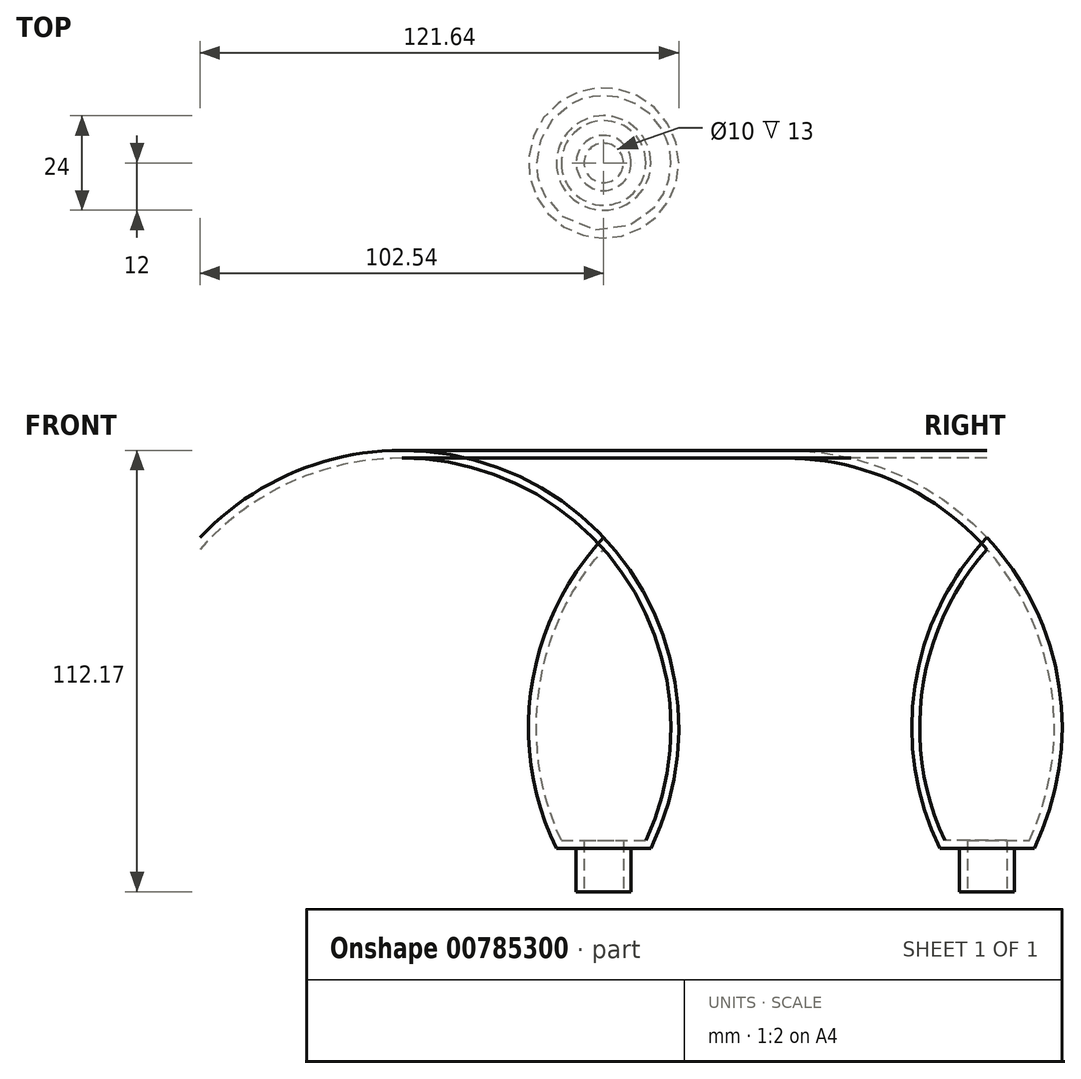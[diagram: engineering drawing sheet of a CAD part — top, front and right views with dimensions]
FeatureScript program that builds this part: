
annotation { "Feature Type Name" : "Feature", "Feature Type Description" : "" }
export const myFeature = defineFeature(function(context is Context, id is Id, definition is map)
    precondition{}
    {
        {
            var Q0;
            Q0=qCreatedBy(makeId("Front.planeOp"),FACE);
            var sketch = newSketch(context, id + "F0", { "sketchPlane" : qUnion([Q0])});
            skLineSegment(sketch, "E0", {"start": v(0, 0) * mm, "end": v(0, 90) * mm});
            skLineSegment(sketch, "E1", {"start": v(5, 0) * mm, "end": v(22.78, 0) * mm});
            skLineSegment(sketch, "E2", {"start": v(5, 0) * mm, "end": v(5, 13) * mm});
            skLineSegment(sketch, "E3", {"start": v(5, 13) * mm, "end": v(10.74, 13) * mm});
            skArc(sketch, "E4", {"start": v(10.74, 13) * mm, "mid": v(16.4, 51.61) * mm, "end": v(0, 87.03) * mm});
            skArc(sketch, "E5.0", {"start": v(12, 11) * mm, "mid": v(18.3, 52.37) * mm, "end": v(0, 90) * mm});
            skLineSegment(sketch, "E5.1", {"start": v(7, 11) * mm, "end": v(12, 11) * mm});
            skLineSegment(sketch, "E5.2", {"start": v(7, 0) * mm, "end": v(7, 11) * mm});
            skLineSegment(sketch, "E6", {"start": v(7, 0) * mm, "end": v(5, 0) * mm});
            skSolve(sketch);
        }
        {
            var Q0;
            {var subQ1=sQuery(id+"F0.wireOp",EDGE,"E2");Q0=makeQuery(id+"F0.imprint","IMPRINT",FACE,{"disambiguationData":[TD([[makeQuery(id+"F0.imprint","IMPRINT",EDGE,{"derivedFrom":subQ1}),-1.0]])]});}
            var Q1;
            Q1=sQuery(id+"F0.wireOp",EDGE,"E0");
            revolve(context, id + "F1", {"surfaceOperationType" : NewSurfaceOperationType.NEW, "entities" : qUnion([Q0]), "axis" : qUnion([Q1]), "revolveType" : RevolveType.FULL});
        }
    });
